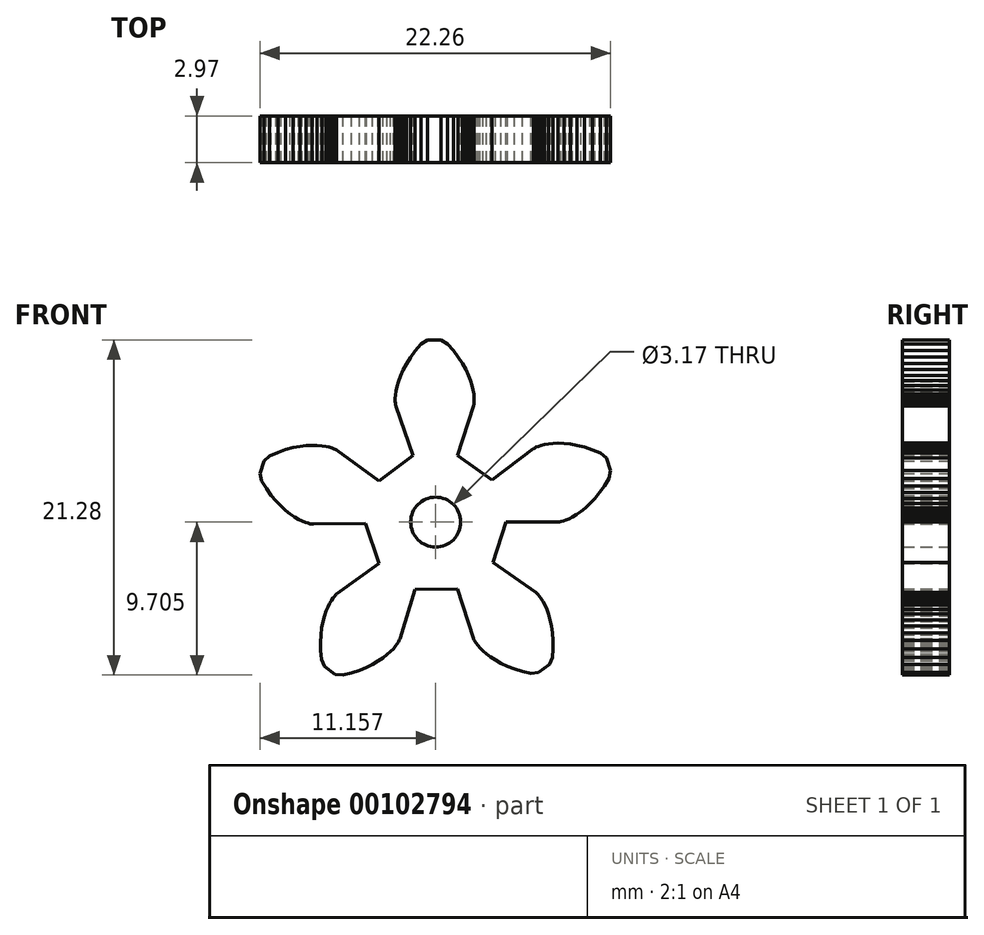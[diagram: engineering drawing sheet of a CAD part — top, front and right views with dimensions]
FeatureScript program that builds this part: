
annotation { "Feature Type Name" : "Feature", "Feature Type Description" : "" }
export const myFeature = defineFeature(function(context is Context, id is Id, definition is map)
    precondition{}
    {
        {
            var Q0;
            Q0=qCreatedBy(makeId("Front.planeOp"),FACE);
            var sketch = newSketch(context, id + "F0", { "sketchPlane" : qUnion([Q0])});
            skLineSegment(sketch, "E0", {"start": v(4.5, -0.93) * mm, "end": v(7.8, -0.93) * mm});
            skLineSegment(sketch, "E1", {"start": v(7.8, -0.93) * mm, "end": v(7.83, -0.93) * mm});
            skLineSegment(sketch, "E2", {"start": v(7.83, -0.93) * mm, "end": v(7.9, -0.93) * mm});
            skLineSegment(sketch, "E3", {"start": v(7.9, -0.93) * mm, "end": v(8, -0.9) * mm});
            skLineSegment(sketch, "E4", {"start": v(8, -0.9) * mm, "end": v(8.13, -0.87) * mm});
            skLineSegment(sketch, "E5", {"start": v(8.13, -0.87) * mm, "end": v(8.3, -0.8) * mm});
            skLineSegment(sketch, "E6", {"start": v(8.3, -0.8) * mm, "end": v(8.5, -0.72) * mm});
            skLineSegment(sketch, "E7", {"start": v(8.5, -0.72) * mm, "end": v(8.73, -0.6) * mm});
            skLineSegment(sketch, "E8", {"start": v(8.73, -0.6) * mm, "end": v(8.98, -0.46) * mm});
            skLineSegment(sketch, "E9", {"start": v(8.98, -0.46) * mm, "end": v(9.25, -0.27) * mm});
            skLineSegment(sketch, "E10", {"start": v(9.25, -0.27) * mm, "end": v(9.54, -0.03) * mm});
            skLineSegment(sketch, "E11", {"start": v(9.54, -0.03) * mm, "end": v(9.84, 0.24) * mm});
            skLineSegment(sketch, "E12", {"start": v(9.84, 0.24) * mm, "end": v(10.14, 0.57) * mm});
            skLineSegment(sketch, "E13", {"start": v(10.14, 0.57) * mm, "end": v(10.44, 0.94) * mm});
            skLineSegment(sketch, "E14", {"start": v(10.44, 0.94) * mm, "end": v(10.74, 1.37) * mm});
            skLineSegment(sketch, "E15", {"start": v(10.74, 1.37) * mm, "end": v(11.03, 1.85) * mm});
            skLineSegment(sketch, "E16", {"start": v(11.03, 1.85) * mm, "end": v(11.13, 2.33) * mm});
            skLineSegment(sketch, "E17", {"start": v(11.13, 2.33) * mm, "end": v(10.87, 3.13) * mm});
            skLineSegment(sketch, "E18", {"start": v(10.87, 3.13) * mm, "end": v(10.5, 3.45) * mm});
            skLineSegment(sketch, "E19", {"start": v(10.5, 3.45) * mm, "end": v(9.98, 3.66) * mm});
            skLineSegment(sketch, "E20", {"start": v(9.98, 3.66) * mm, "end": v(9.48, 3.82) * mm});
            skLineSegment(sketch, "E21", {"start": v(9.48, 3.82) * mm, "end": v(9.01, 3.94) * mm});
            skLineSegment(sketch, "E22", {"start": v(9.01, 3.94) * mm, "end": v(8.57, 4.02) * mm});
            skLineSegment(sketch, "E23", {"start": v(8.57, 4.02) * mm, "end": v(8.17, 4.06) * mm});
            skLineSegment(sketch, "E24", {"start": v(8.17, 4.06) * mm, "end": v(7.8, 4.08) * mm});
            skLineSegment(sketch, "E25", {"start": v(7.8, 4.08) * mm, "end": v(7.47, 4.06) * mm});
            skLineSegment(sketch, "E26", {"start": v(7.47, 4.06) * mm, "end": v(7.18, 4.03) * mm});
            skLineSegment(sketch, "E27", {"start": v(7.18, 4.03) * mm, "end": v(6.93, 4) * mm});
            skLineSegment(sketch, "E28", {"start": v(6.93, 4) * mm, "end": v(6.71, 3.94) * mm});
            skLineSegment(sketch, "E29", {"start": v(6.71, 3.94) * mm, "end": v(6.54, 3.88) * mm});
            skLineSegment(sketch, "E30", {"start": v(6.54, 3.88) * mm, "end": v(6.41, 3.83) * mm});
            skLineSegment(sketch, "E31", {"start": v(6.41, 3.83) * mm, "end": v(6.32, 3.78) * mm});
            skLineSegment(sketch, "E32", {"start": v(6.32, 3.78) * mm, "end": v(6.26, 3.75) * mm});
            skLineSegment(sketch, "E33", {"start": v(6.26, 3.75) * mm, "end": v(6.24, 3.74) * mm});
            skLineSegment(sketch, "E34", {"start": v(6.24, 3.74) * mm, "end": v(3.6, 1.75) * mm});
            skLineSegment(sketch, "E35", {"start": v(3.6, 1.75) * mm, "end": v(1.4, 3.31) * mm});
            skLineSegment(sketch, "E36", {"start": v(1.4, 3.31) * mm, "end": v(2.43, 6.46) * mm});
            skLineSegment(sketch, "E37", {"start": v(2.43, 6.46) * mm, "end": v(2.44, 6.48) * mm});
            skLineSegment(sketch, "E38", {"start": v(2.44, 6.48) * mm, "end": v(2.45, 6.55) * mm});
            skLineSegment(sketch, "E39", {"start": v(2.45, 6.55) * mm, "end": v(2.46, 6.65) * mm});
            skLineSegment(sketch, "E40", {"start": v(2.46, 6.65) * mm, "end": v(2.47, 6.8) * mm});
            skLineSegment(sketch, "E41", {"start": v(2.47, 6.8) * mm, "end": v(2.46, 6.97) * mm});
            skLineSegment(sketch, "E42", {"start": v(2.46, 6.97) * mm, "end": v(2.45, 7.19) * mm});
            skLineSegment(sketch, "E43", {"start": v(2.45, 7.19) * mm, "end": v(2.4, 7.44) * mm});
            skLineSegment(sketch, "E44", {"start": v(2.4, 7.44) * mm, "end": v(2.34, 7.73) * mm});
            skLineSegment(sketch, "E45", {"start": v(2.34, 7.73) * mm, "end": v(2.24, 8.04) * mm});
            skLineSegment(sketch, "E46", {"start": v(2.24, 8.04) * mm, "end": v(2.1, 8.39) * mm});
            skLineSegment(sketch, "E47", {"start": v(2.1, 8.39) * mm, "end": v(1.94, 8.76) * mm});
            skLineSegment(sketch, "E48", {"start": v(1.94, 8.76) * mm, "end": v(1.72, 9.15) * mm});
            skLineSegment(sketch, "E49", {"start": v(1.72, 9.15) * mm, "end": v(1.46, 9.55) * mm});
            skLineSegment(sketch, "E50", {"start": v(1.46, 9.55) * mm, "end": v(1.14, 9.97) * mm});
            skLineSegment(sketch, "E51", {"start": v(1.14, 9.97) * mm, "end": v(0.78, 10.39) * mm});
            skLineSegment(sketch, "E52", {"start": v(0.78, 10.39) * mm, "end": v(0.35, 10.64) * mm});
            skLineSegment(sketch, "E53", {"start": v(0.35, 10.64) * mm, "end": v(-0.49, 10.63) * mm});
            skLineSegment(sketch, "E54", {"start": v(-0.49, 10.63) * mm, "end": v(-0.91, 10.37) * mm});
            skLineSegment(sketch, "E55", {"start": v(-0.91, 10.37) * mm, "end": v(-1.27, 9.95) * mm});
            skLineSegment(sketch, "E56", {"start": v(-1.27, 9.95) * mm, "end": v(-1.58, 9.53) * mm});
            skLineSegment(sketch, "E57", {"start": v(-1.58, 9.53) * mm, "end": v(-1.83, 9.12) * mm});
            skLineSegment(sketch, "E58", {"start": v(-1.83, 9.12) * mm, "end": v(-2.04, 8.73) * mm});
            skLineSegment(sketch, "E59", {"start": v(-2.04, 8.73) * mm, "end": v(-2.2, 8.35) * mm});
            skLineSegment(sketch, "E60", {"start": v(-2.2, 8.35) * mm, "end": v(-2.34, 8) * mm});
            skLineSegment(sketch, "E61", {"start": v(-2.34, 8) * mm, "end": v(-2.43, 7.69) * mm});
            skLineSegment(sketch, "E62", {"start": v(-2.43, 7.69) * mm, "end": v(-2.49, 7.4) * mm});
            skLineSegment(sketch, "E63", {"start": v(-2.49, 7.4) * mm, "end": v(-2.53, 7.15) * mm});
            skLineSegment(sketch, "E64", {"start": v(-2.53, 7.15) * mm, "end": v(-2.54, 6.93) * mm});
            skLineSegment(sketch, "E65", {"start": v(-2.54, 6.93) * mm, "end": v(-2.54, 6.75) * mm});
            skLineSegment(sketch, "E66", {"start": v(-2.54, 6.75) * mm, "end": v(-2.53, 6.6) * mm});
            skLineSegment(sketch, "E67", {"start": v(-2.53, 6.6) * mm, "end": v(-2.52, 6.5) * mm});
            skLineSegment(sketch, "E68", {"start": v(-2.52, 6.5) * mm, "end": v(-2.5, 6.44) * mm});
            skLineSegment(sketch, "E69", {"start": v(-2.5, 6.44) * mm, "end": v(-2.5, 6.41) * mm});
            skLineSegment(sketch, "E70", {"start": v(-2.5, 6.41) * mm, "end": v(-1.42, 3.29) * mm});
            skLineSegment(sketch, "E71", {"start": v(-1.42, 3.29) * mm, "end": v(-3.58, 1.69) * mm});
            skLineSegment(sketch, "E72", {"start": v(-3.58, 1.69) * mm, "end": v(-6.26, 3.63) * mm});
            skLineSegment(sketch, "E73", {"start": v(-6.26, 3.63) * mm, "end": v(-6.28, 3.65) * mm});
            skLineSegment(sketch, "E74", {"start": v(-6.28, 3.65) * mm, "end": v(-6.34, 3.68) * mm});
            skLineSegment(sketch, "E75", {"start": v(-6.34, 3.68) * mm, "end": v(-6.44, 3.72) * mm});
            skLineSegment(sketch, "E76", {"start": v(-6.44, 3.72) * mm, "end": v(-6.57, 3.77) * mm});
            skLineSegment(sketch, "E77", {"start": v(-6.57, 3.77) * mm, "end": v(-6.74, 3.83) * mm});
            skLineSegment(sketch, "E78", {"start": v(-6.74, 3.83) * mm, "end": v(-6.95, 3.88) * mm});
            skLineSegment(sketch, "E79", {"start": v(-6.95, 3.88) * mm, "end": v(-7.2, 3.92) * mm});
            skLineSegment(sketch, "E80", {"start": v(-7.2, 3.92) * mm, "end": v(-7.5, 3.94) * mm});
            skLineSegment(sketch, "E81", {"start": v(-7.5, 3.94) * mm, "end": v(-7.83, 3.95) * mm});
            skLineSegment(sketch, "E82", {"start": v(-7.83, 3.95) * mm, "end": v(-8.2, 3.93) * mm});
            skLineSegment(sketch, "E83", {"start": v(-8.2, 3.93) * mm, "end": v(-8.6, 3.88) * mm});
            skLineSegment(sketch, "E84", {"start": v(-8.6, 3.88) * mm, "end": v(-9.04, 3.8) * mm});
            skLineSegment(sketch, "E85", {"start": v(-9.04, 3.8) * mm, "end": v(-9.5, 3.67) * mm});
            skLineSegment(sketch, "E86", {"start": v(-9.5, 3.67) * mm, "end": v(-10, 3.5) * mm});
            skLineSegment(sketch, "E87", {"start": v(-10, 3.5) * mm, "end": v(-10.51, 3.28) * mm});
            skLineSegment(sketch, "E88", {"start": v(-10.51, 3.28) * mm, "end": v(-10.88, 2.95) * mm});
            skLineSegment(sketch, "E89", {"start": v(-10.88, 2.95) * mm, "end": v(-11.13, 2.15) * mm});
            skLineSegment(sketch, "E90", {"start": v(-11.13, 2.15) * mm, "end": v(-11.02, 1.67) * mm});
            skLineSegment(sketch, "E91", {"start": v(-11.02, 1.67) * mm, "end": v(-10.72, 1.2) * mm});
            skLineSegment(sketch, "E92", {"start": v(-10.72, 1.2) * mm, "end": v(-10.42, 0.77) * mm});
            skLineSegment(sketch, "E93", {"start": v(-10.42, 0.77) * mm, "end": v(-10.1, 0.4) * mm});
            skLineSegment(sketch, "E94", {"start": v(-10.1, 0.4) * mm, "end": v(-9.8, 0.08) * mm});
            skLineSegment(sketch, "E95", {"start": v(-9.8, 0.08) * mm, "end": v(-9.5, -0.2) * mm});
            skLineSegment(sketch, "E96", {"start": v(-9.5, -0.2) * mm, "end": v(-9.2, -0.42) * mm});
            skLineSegment(sketch, "E97", {"start": v(-9.2, -0.42) * mm, "end": v(-8.93, -0.6) * mm});
            skLineSegment(sketch, "E98", {"start": v(-8.93, -0.6) * mm, "end": v(-8.68, -0.75) * mm});
            skLineSegment(sketch, "E99", {"start": v(-8.68, -0.75) * mm, "end": v(-8.45, -0.86) * mm});
            skLineSegment(sketch, "E100", {"start": v(-8.45, -0.86) * mm, "end": v(-8.25, -0.95) * mm});
            skLineSegment(sketch, "E101", {"start": v(-8.25, -0.95) * mm, "end": v(-8.08, -1) * mm});
            skLineSegment(sketch, "E102", {"start": v(-8.08, -1) * mm, "end": v(-7.94, -1.04) * mm});
            skLineSegment(sketch, "E103", {"start": v(-7.94, -1.04) * mm, "end": v(-7.84, -1.05) * mm});
            skLineSegment(sketch, "E104", {"start": v(-7.84, -1.05) * mm, "end": v(-7.77, -1.06) * mm});
            skLineSegment(sketch, "E105", {"start": v(-7.77, -1.06) * mm, "end": v(-7.74, -1.06) * mm});
            skLineSegment(sketch, "E106", {"start": v(-7.74, -1.06) * mm, "end": v(-4.44, -1) * mm});
            skLineSegment(sketch, "E107", {"start": v(-4.44, -1) * mm, "end": v(-3.58, -3.56) * mm});
            skLineSegment(sketch, "E108", {"start": v(-3.58, -3.56) * mm, "end": v(-6.26, -5.5) * mm});
            skLineSegment(sketch, "E109", {"start": v(-6.26, -5.5) * mm, "end": v(-6.28, -5.52) * mm});
            skLineSegment(sketch, "E110", {"start": v(-6.28, -5.52) * mm, "end": v(-6.33, -5.57) * mm});
            skLineSegment(sketch, "E111", {"start": v(-6.33, -5.57) * mm, "end": v(-6.4, -5.64) * mm});
            skLineSegment(sketch, "E112", {"start": v(-6.4, -5.64) * mm, "end": v(-6.49, -5.75) * mm});
            skLineSegment(sketch, "E113", {"start": v(-6.49, -5.75) * mm, "end": v(-6.6, -5.9) * mm});
            skLineSegment(sketch, "E114", {"start": v(-6.6, -5.9) * mm, "end": v(-6.7, -6.09) * mm});
            skLineSegment(sketch, "E115", {"start": v(-6.7, -6.09) * mm, "end": v(-6.82, -6.31) * mm});
            skLineSegment(sketch, "E116", {"start": v(-6.82, -6.31) * mm, "end": v(-6.93, -6.58) * mm});
            skLineSegment(sketch, "E117", {"start": v(-6.93, -6.58) * mm, "end": v(-7.04, -6.9) * mm});
            skLineSegment(sketch, "E118", {"start": v(-7.04, -6.9) * mm, "end": v(-7.14, -7.25) * mm});
            skLineSegment(sketch, "E119", {"start": v(-7.14, -7.25) * mm, "end": v(-7.22, -7.65) * mm});
            skLineSegment(sketch, "E120", {"start": v(-7.22, -7.65) * mm, "end": v(-7.27, -8.1) * mm});
            skLineSegment(sketch, "E121", {"start": v(-7.27, -8.1) * mm, "end": v(-7.3, -8.58) * mm});
            skLineSegment(sketch, "E122", {"start": v(-7.3, -8.58) * mm, "end": v(-7.28, -9.1) * mm});
            skLineSegment(sketch, "E123", {"start": v(-7.28, -9.1) * mm, "end": v(-7.24, -9.66) * mm});
            skLineSegment(sketch, "E124", {"start": v(-7.24, -9.66) * mm, "end": v(-7.04, -10.1) * mm});
            skLineSegment(sketch, "E125", {"start": v(-7.04, -10.1) * mm, "end": v(-6.35, -10.6) * mm});
            skLineSegment(sketch, "E126", {"start": v(-6.35, -10.6) * mm, "end": v(-5.86, -10.64) * mm});
            skLineSegment(sketch, "E127", {"start": v(-5.86, -10.64) * mm, "end": v(-5.32, -10.5) * mm});
            skLineSegment(sketch, "E128", {"start": v(-5.32, -10.5) * mm, "end": v(-4.83, -10.34) * mm});
            skLineSegment(sketch, "E129", {"start": v(-4.83, -10.34) * mm, "end": v(-4.38, -10.16) * mm});
            skLineSegment(sketch, "E130", {"start": v(-4.38, -10.16) * mm, "end": v(-3.98, -9.97) * mm});
            skLineSegment(sketch, "E131", {"start": v(-3.98, -9.97) * mm, "end": v(-3.62, -9.76) * mm});
            skLineSegment(sketch, "E132", {"start": v(-3.62, -9.76) * mm, "end": v(-3.32, -9.56) * mm});
            skLineSegment(sketch, "E133", {"start": v(-3.32, -9.56) * mm, "end": v(-3.06, -9.35) * mm});
            skLineSegment(sketch, "E134", {"start": v(-3.06, -9.35) * mm, "end": v(-2.84, -9.16) * mm});
            skLineSegment(sketch, "E135", {"start": v(-2.84, -9.16) * mm, "end": v(-2.66, -8.97) * mm});
            skLineSegment(sketch, "E136", {"start": v(-2.66, -8.97) * mm, "end": v(-2.52, -8.8) * mm});
            skLineSegment(sketch, "E137", {"start": v(-2.52, -8.8) * mm, "end": v(-2.41, -8.66) * mm});
            skLineSegment(sketch, "E138", {"start": v(-2.41, -8.66) * mm, "end": v(-2.34, -8.54) * mm});
            skLineSegment(sketch, "E139", {"start": v(-2.34, -8.54) * mm, "end": v(-2.29, -8.45) * mm});
            skLineSegment(sketch, "E140", {"start": v(-2.29, -8.45) * mm, "end": v(-2.26, -8.4) * mm});
            skLineSegment(sketch, "E141", {"start": v(-2.26, -8.4) * mm, "end": v(-2.25, -8.36) * mm});
            skLineSegment(sketch, "E142", {"start": v(-2.25, -8.36) * mm, "end": v(-1.28, -5.2) * mm});
            skLineSegment(sketch, "E143", {"start": v(-1.28, -5.2) * mm, "end": v(1.4, -5.18) * mm});
            skLineSegment(sketch, "E144", {"start": v(1.4, -5.18) * mm, "end": v(2.43, -8.33) * mm});
            skLineSegment(sketch, "E145", {"start": v(2.43, -8.33) * mm, "end": v(2.44, -8.35) * mm});
            skLineSegment(sketch, "E146", {"start": v(2.44, -8.35) * mm, "end": v(2.47, -8.41) * mm});
            skLineSegment(sketch, "E147", {"start": v(2.47, -8.41) * mm, "end": v(2.52, -8.5) * mm});
            skLineSegment(sketch, "E148", {"start": v(2.52, -8.5) * mm, "end": v(2.6, -8.62) * mm});
            skLineSegment(sketch, "E149", {"start": v(2.6, -8.62) * mm, "end": v(2.7, -8.77) * mm});
            skLineSegment(sketch, "E150", {"start": v(2.7, -8.77) * mm, "end": v(2.85, -8.93) * mm});
            skLineSegment(sketch, "E151", {"start": v(2.85, -8.93) * mm, "end": v(3.03, -9.1) * mm});
            skLineSegment(sketch, "E152", {"start": v(3.03, -9.1) * mm, "end": v(3.25, -9.3) * mm});
            skLineSegment(sketch, "E153", {"start": v(3.25, -9.3) * mm, "end": v(3.51, -9.5) * mm});
            skLineSegment(sketch, "E154", {"start": v(3.51, -9.5) * mm, "end": v(3.82, -9.7) * mm});
            skLineSegment(sketch, "E155", {"start": v(3.82, -9.7) * mm, "end": v(4.18, -9.9) * mm});
            skLineSegment(sketch, "E156", {"start": v(4.18, -9.9) * mm, "end": v(4.58, -10.09) * mm});
            skLineSegment(sketch, "E157", {"start": v(4.58, -10.09) * mm, "end": v(5.03, -10.26) * mm});
            skLineSegment(sketch, "E158", {"start": v(5.03, -10.26) * mm, "end": v(5.53, -10.41) * mm});
            skLineSegment(sketch, "E159", {"start": v(5.53, -10.41) * mm, "end": v(6.08, -10.54) * mm});
            skLineSegment(sketch, "E160", {"start": v(6.08, -10.54) * mm, "end": v(6.57, -10.49) * mm});
            skLineSegment(sketch, "E161", {"start": v(6.57, -10.49) * mm, "end": v(7.24, -9.99) * mm});
            skLineSegment(sketch, "E162", {"start": v(7.24, -9.99) * mm, "end": v(7.43, -9.53) * mm});
            skLineSegment(sketch, "E163", {"start": v(7.43, -9.53) * mm, "end": v(7.47, -8.98) * mm});
            skLineSegment(sketch, "E164", {"start": v(7.47, -8.98) * mm, "end": v(7.47, -8.46) * mm});
            skLineSegment(sketch, "E165", {"start": v(7.47, -8.46) * mm, "end": v(7.44, -7.97) * mm});
            skLineSegment(sketch, "E166", {"start": v(7.44, -7.97) * mm, "end": v(7.38, -7.53) * mm});
            skLineSegment(sketch, "E167", {"start": v(7.38, -7.53) * mm, "end": v(7.3, -7.13) * mm});
            skLineSegment(sketch, "E168", {"start": v(7.3, -7.13) * mm, "end": v(7.2, -6.78) * mm});
            skLineSegment(sketch, "E169", {"start": v(7.2, -6.78) * mm, "end": v(7.08, -6.47) * mm});
            skLineSegment(sketch, "E170", {"start": v(7.08, -6.47) * mm, "end": v(6.96, -6.2) * mm});
            skLineSegment(sketch, "E171", {"start": v(6.96, -6.2) * mm, "end": v(6.84, -5.97) * mm});
            skLineSegment(sketch, "E172", {"start": v(6.84, -5.97) * mm, "end": v(6.73, -5.79) * mm});
            skLineSegment(sketch, "E173", {"start": v(6.73, -5.79) * mm, "end": v(6.62, -5.64) * mm});
            skLineSegment(sketch, "E174", {"start": v(6.62, -5.64) * mm, "end": v(6.53, -5.53) * mm});
            skLineSegment(sketch, "E175", {"start": v(6.53, -5.53) * mm, "end": v(6.46, -5.46) * mm});
            skLineSegment(sketch, "E176", {"start": v(6.46, -5.46) * mm, "end": v(6.4, -5.41) * mm});
            skLineSegment(sketch, "E177", {"start": v(6.4, -5.41) * mm, "end": v(6.39, -5.4) * mm});
            skLineSegment(sketch, "E178", {"start": v(6.39, -5.4) * mm, "end": v(3.68, -3.5) * mm});
            skLineSegment(sketch, "E179", {"start": v(3.68, -3.5) * mm, "end": v(4.5, -0.93) * mm});
            skCircle(sketch, "E180", {"center": v(0.03, -0.93) * mm, "radius": 4.46 * mm});
            skCircle(sketch, "E181", {"center": v(0.03, -0.93) * mm, "radius": 1.59 * mm});
            skSolve(sketch);
        }
        {
            var Q0;
            {var subQ0=sQuery(id+"F0.wireOp",EDGE,"E72");Q0=makeQuery(id+"F0.imprint","IMPRINT",FACE,{"disambiguationData":[TD([[makeQuery(id+"F0.imprint","IMPRINT",EDGE,{"derivedFrom":subQ0}),1.0]])]});}
            var Q1;
            {var subQ15=sQuery(id+"F0.wireOp",EDGE,"E35");Q1=makeQuery(id+"F0.imprint","IMPRINT",FACE,{"disambiguationData":[TD([[makeQuery(id+"F0.imprint","IMPRINT",EDGE,{"derivedFrom":subQ15}),1.0]])]});}
            var Q2;
            {var subQ1=sQuery(id+"F0.wireOp",EDGE,"E37");Q2=makeQuery(id+"F0.imprint","IMPRINT",FACE,{"disambiguationData":[TD([[makeQuery(id+"F0.imprint","IMPRINT",EDGE,{"derivedFrom":subQ1}),1.0]])]});}
            var Q3;
            {var subQ0=sQuery(id+"F0.wireOp",EDGE,"E0");Q3=makeQuery(id+"F0.imprint","IMPRINT",FACE,{"disambiguationData":[TD([[makeQuery(id+"F0.imprint","IMPRINT",EDGE,{"derivedFrom":subQ0}),1.0]])]});}
            var Q4;
            {var subQ0=sQuery(id+"F0.wireOp",EDGE,"E145");Q4=makeQuery(id+"F0.imprint","IMPRINT",FACE,{"disambiguationData":[TD([[makeQuery(id+"F0.imprint","IMPRINT",EDGE,{"derivedFrom":subQ0}),1.0]])]});}
            var Q5;
            {var subQ0=sQuery(id+"F0.wireOp",EDGE,"E108");Q5=makeQuery(id+"F0.imprint","IMPRINT",FACE,{"disambiguationData":[TD([[makeQuery(id+"F0.imprint","IMPRINT",EDGE,{"derivedFrom":subQ0}),1.0]])]});}
            extrude(context, id + "F1", {"entities" : qUnion([Q0, Q1, Q2, Q3, Q4, Q5]), "depth" : 2.97 * mm});
        }
    });
